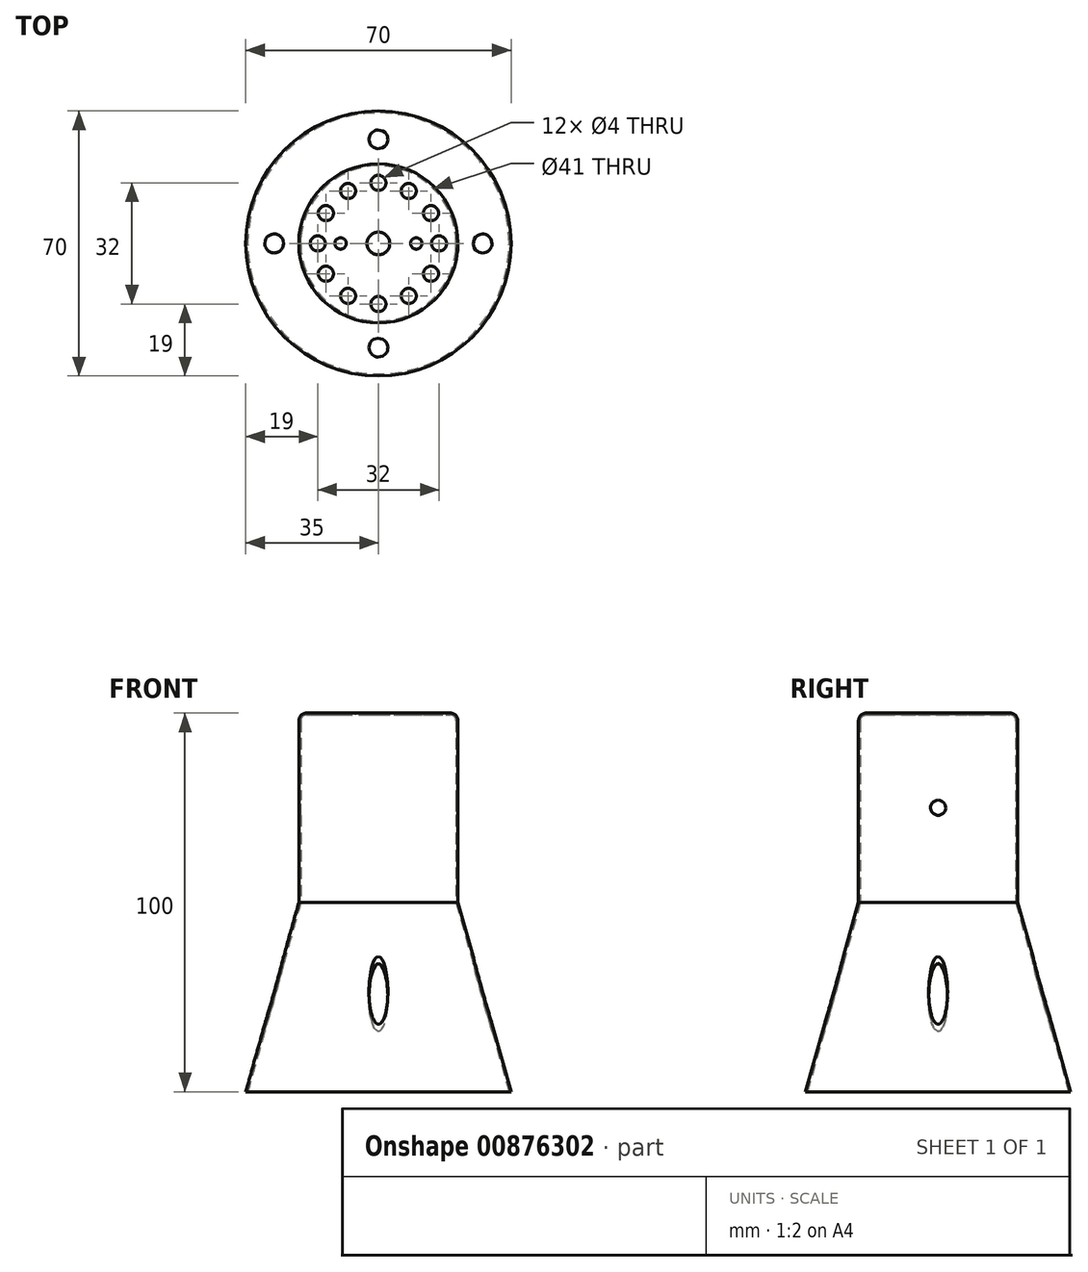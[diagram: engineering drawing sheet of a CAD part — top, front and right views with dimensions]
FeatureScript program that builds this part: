
annotation { "Feature Type Name" : "Feature", "Feature Type Description" : "" }
export const myFeature = defineFeature(function(context is Context, id is Id, definition is map)
    precondition{}
    {
        {
            var Q0;
            Q0=qCreatedBy(makeId("Front.planeOp"),FACE);
            var sketch = newSketch(context, id + "F0", { "sketchPlane" : qUnion([Q0])});
            skLineSegment(sketch, "E0", {"start": v(0, 0) * mm, "end": v(0, 50) * mm});
            skLineSegment(sketch, "E1", {"start": v(0, 0) * mm, "end": v(0, -50) * mm});
            skLineSegment(sketch, "E2.bottom", {"start": v(35, 0) * mm, "end": v(-35, 0) * mm});
            skLineSegment(sketch, "E2.top", {"start": v(35, -50) * mm, "end": v(-35, -50) * mm});
            skLineSegment(sketch, "E2.left", {"start": v(35, 0) * mm, "end": v(35, -50) * mm});
            skLineSegment(sketch, "E2.right", {"start": v(-35, 0) * mm, "end": v(-35, -50) * mm});
            skPoint(sketch, "E2.middle", {"position": v(0, -25) * mm});
            skLineSegment(sketch, "E3.bottom", {"start": v(21, 50) * mm, "end": v(-21, 50) * mm});
            skLineSegment(sketch, "E3.top", {"start": v(21, 0) * mm, "end": v(-21, 0) * mm});
            skLineSegment(sketch, "E3.left", {"start": v(21, 50) * mm, "end": v(21, 0) * mm});
            skLineSegment(sketch, "E3.right", {"start": v(-21, 50) * mm, "end": v(-21, 0) * mm});
            skPoint(sketch, "E3.middle", {"position": v(0, 25) * mm});
            skLineSegment(sketch, "E4", {"start": v(-21, 0) * mm, "end": v(-35, -50) * mm});
            skLineSegment(sketch, "E5", {"start": v(21, 0) * mm, "end": v(35, -50) * mm});
            skSolve(sketch);
        }
        {
            var Q0;
            {var subQ0=sQuery(id+"F0.wireOp",EDGE,"E0");Q0=makeQuery(id+"F0.imprint","IMPRINT",FACE,{"disambiguationData":[TD([[makeQuery(id+"F0.imprint","IMPRINT",EDGE,{"derivedFrom":subQ0}),1.0]])]});}
            var Q1;
            {var subQ0=sQuery(id+"F0.wireOp",EDGE,"E1");Q1=makeQuery(id+"F0.imprint","IMPRINT",FACE,{"disambiguationData":[TD([[makeQuery(id+"F0.imprint","IMPRINT",EDGE,{"derivedFrom":subQ0}),-1.0]])]});}
            var Q2;
            Q2=sQuery(id+"F0.wireOp",EDGE,"E3.right");
            var Q3;
            Q3=sQuery(id+"F0.wireOp",EDGE,"E4");
            var Q4;
            Q4=sQuery(id+"F0.wireOp",EDGE,"E0");
            revolve(context, id + "F1", {"surfaceOperationType" : NewSurfaceOperationType.NEW, "entities" : qUnion([Q0, Q1]), "surfaceEntities" : qUnion([Q2, Q3]), "axis" : qUnion([Q4]), "revolveType" : RevolveType.FULL});
        }
        {
            var Q0;
            Q0=makeQuery(id+"F1.opRevolve","SWEPT_EDGE",EDGE,{"disambiguationData":[OSD([sQuery(id+"F0.wireOp",EDGE,"E3.bottom"),sQuery(id+"F0.wireOp",EDGE,"E3.right")])]});
            fillet(context, id + "F2", {"entities" : qUnion([Q0]), "radius" : 2 * mm, "tangentPropagation" : true, "allowEdgeOverflow" : false});
        }
        {
            var Q0;
            Q0=makeQuery(id+"F1.opRevolve","SWEPT_FACE",FACE,{"disambiguationData":[OSD([sQuery(id+"F0.wireOp",EDGE,"E2.top")])]});
            shell(context, id + "F3", {"entities" : qUnion([Q0]), "thickness" : 0.5 * mm});
        }
        {
            var Q0;
            Q0=qCreatedBy(makeId("Top.planeOp"),FACE);
            var sketch = newSketch(context, id + "F4", { "sketchPlane" : qUnion([Q0])});
            skCircle(sketch, "E6", {"center": v(0, 0) * mm, "radius": 27.5 * mm});
            skCircle(sketch, "E7", {"center": v(0, 27.5) * mm, "radius": 2.5 * mm});
            skCircle(sketch, "E8", {"center": v(0, -27.5) * mm, "radius": 2.5 * mm});
            skCircle(sketch, "E9", {"center": v(27.5, 0) * mm, "radius": 2.5 * mm});
            skCircle(sketch, "E10", {"center": v(-27.5, 0) * mm, "radius": 2.5 * mm});
            skSolve(sketch);
        }
        {
            var Q0;
            {var subQ0=sQuery(id+"F4.wireOp",EDGE,"E7");var subQ1=sQuery(id+"F4.wireOp",EDGE,"E6");var subQ2=makeQuery(id+"F4.imprint","INTERSECT",VERTEX,{"disambiguationData":[OD(0.0)],"derivedFrom":[subQ1,subQ0]});Q0=makeQuery(id+"F4.imprint","IMPRINT",FACE,{"disambiguationData":[TD([[makeQuery(id+"F4.imprint","IMPRINT",EDGE,{"disambiguationData":[TD([[subQ2,-1.0]])],"derivedFrom":subQ1}),-1.0]])]});}
            var Q1;
            {var subQ0=sQuery(id+"F4.wireOp",EDGE,"E7");var subQ1=sQuery(id+"F4.wireOp",EDGE,"E6");var subQ2=makeQuery(id+"F4.imprint","INTERSECT",VERTEX,{"disambiguationData":[OD(0.0)],"derivedFrom":[subQ1,subQ0]});Q1=makeQuery(id+"F4.imprint","IMPRINT",FACE,{"disambiguationData":[TD([[makeQuery(id+"F4.imprint","IMPRINT",EDGE,{"disambiguationData":[TD([[subQ2,-1.0]])],"derivedFrom":subQ1}),1.0]])]});}
            var Q2;
            {var subQ0=sQuery(id+"F4.wireOp",EDGE,"E10");var subQ1=sQuery(id+"F4.wireOp",EDGE,"E6");var subQ2=makeQuery(id+"F4.imprint","INTERSECT",VERTEX,{"disambiguationData":[OD(0.0)],"derivedFrom":[subQ1,subQ0]});Q2=makeQuery(id+"F4.imprint","IMPRINT",FACE,{"disambiguationData":[TD([[makeQuery(id+"F4.imprint","IMPRINT",EDGE,{"disambiguationData":[TD([[subQ2,-1.0]])],"derivedFrom":subQ1}),1.0]])]});}
            var Q3;
            {var subQ0=sQuery(id+"F4.wireOp",EDGE,"E10");var subQ1=sQuery(id+"F4.wireOp",EDGE,"E6");var subQ2=makeQuery(id+"F4.imprint","INTERSECT",VERTEX,{"disambiguationData":[OD(0.0)],"derivedFrom":[subQ1,subQ0]});Q3=makeQuery(id+"F4.imprint","IMPRINT",FACE,{"disambiguationData":[TD([[makeQuery(id+"F4.imprint","IMPRINT",EDGE,{"disambiguationData":[TD([[subQ2,-1.0]])],"derivedFrom":subQ1}),-1.0]])]});}
            var Q4;
            {var subQ0=sQuery(id+"F4.wireOp",EDGE,"E9");var subQ1=sQuery(id+"F4.wireOp",EDGE,"E6");var subQ2=makeQuery(id+"F4.imprint","INTERSECT",VERTEX,{"disambiguationData":[OD(0.0)],"derivedFrom":[subQ1,subQ0]});Q4=makeQuery(id+"F4.imprint","IMPRINT",FACE,{"disambiguationData":[TD([[makeQuery(id+"F4.imprint","IMPRINT",EDGE,{"disambiguationData":[TD([[subQ2,1.0]])],"derivedFrom":subQ1}),1.0]])]});}
            var Q5;
            {var subQ0=sQuery(id+"F4.wireOp",EDGE,"E9");var subQ1=sQuery(id+"F4.wireOp",EDGE,"E6");var subQ2=makeQuery(id+"F4.imprint","INTERSECT",VERTEX,{"disambiguationData":[OD(0.0)],"derivedFrom":[subQ1,subQ0]});Q5=makeQuery(id+"F4.imprint","IMPRINT",FACE,{"disambiguationData":[TD([[makeQuery(id+"F4.imprint","IMPRINT",EDGE,{"disambiguationData":[TD([[subQ2,1.0]])],"derivedFrom":subQ1}),-1.0]])]});}
            var Q6;
            {var subQ0=sQuery(id+"F4.wireOp",EDGE,"E8");var subQ1=sQuery(id+"F4.wireOp",EDGE,"E6");var subQ2=makeQuery(id+"F4.imprint","INTERSECT",VERTEX,{"disambiguationData":[OD(0.0)],"derivedFrom":[subQ1,subQ0]});Q6=makeQuery(id+"F4.imprint","IMPRINT",FACE,{"disambiguationData":[TD([[makeQuery(id+"F4.imprint","IMPRINT",EDGE,{"disambiguationData":[TD([[subQ2,-1.0]])],"derivedFrom":subQ1}),1.0]])]});}
            var Q7;
            {var subQ0=sQuery(id+"F4.wireOp",EDGE,"E8");var subQ1=sQuery(id+"F4.wireOp",EDGE,"E6");var subQ2=makeQuery(id+"F4.imprint","INTERSECT",VERTEX,{"disambiguationData":[OD(0.0)],"derivedFrom":[subQ1,subQ0]});Q7=makeQuery(id+"F4.imprint","IMPRINT",FACE,{"disambiguationData":[TD([[makeQuery(id+"F4.imprint","IMPRINT",EDGE,{"disambiguationData":[TD([[subQ2,-1.0]])],"derivedFrom":subQ1}),-1.0]])]});}
            extrude(context, id + "F5", {"entities" : qUnion([Q0, Q1, Q2, Q3, Q4, Q5, Q6, Q7]), "operationType" : NewBodyOperationType.REMOVE, "oppositeDirection" : true, "depth" : 63.2 * mm, "offsetDistance" : 25 * mm});
        }
        {
            var Q0;
            Q0=makeQuery(id+"F1.opRevolve","SWEPT_FACE",FACE,{"disambiguationData":[OSD([sQuery(id+"F0.wireOp",EDGE,"E3.bottom")])]});
            var sketch = newSketch(context, id + "F6", { "sketchPlane" : qUnion([Q0])});
            skCircle(sketch, "E11", {"center": v(0, 0) * mm, "radius": 3 * mm});
            skLineSegment(sketch, "E12", {"start": v(0, 0) * mm, "end": v(10, 0) * mm});
            skLineSegment(sketch, "E13", {"start": v(0, 0) * mm, "end": v(-10, 0) * mm});
            skCircle(sketch, "E14", {"center": v(10, 0) * mm, "radius": 1.5 * mm});
            skCircle(sketch, "E15", {"center": v(-10, 0) * mm, "radius": 1.5 * mm});
            skCircle(sketch, "E16", {"center": v(0, 0) * mm, "radius": 16 * mm});
            skCircle(sketch, "E17", {"center": v(0, 16) * mm, "radius": 2 * mm});
            skCircle(sketch, "E18", {"center": v(0, -16) * mm, "radius": 2 * mm});
            skCircle(sketch, "E19", {"center": v(16, 0) * mm, "radius": 2 * mm});
            skCircle(sketch, "E20", {"center": v(-16, 0) * mm, "radius": 2 * mm});
            skLineSegment(sketch, "E21", {"start": v(0, 0) * mm, "end": v(-13.86, 8) * mm});
            skCircle(sketch, "E22", {"center": v(-13.86, 8) * mm, "radius": 2 * mm});
            skLineSegment(sketch, "E23", {"start": v(0, 0) * mm, "end": v(-8, 13.86) * mm});
            skCircle(sketch, "E24", {"center": v(-8, 13.86) * mm, "radius": 2 * mm});
            skLineSegment(sketch, "E25", {"start": v(0, 0) * mm, "end": v(8, 13.86) * mm});
            skCircle(sketch, "E26", {"center": v(8, 13.86) * mm, "radius": 2 * mm});
            skLineSegment(sketch, "E27", {"start": v(0, 0) * mm, "end": v(13.86, 8) * mm});
            skCircle(sketch, "E28", {"center": v(13.86, 8) * mm, "radius": 2 * mm});
            skLineSegment(sketch, "E29", {"start": v(0, 0) * mm, "end": v(13.86, -8) * mm});
            skCircle(sketch, "E30", {"center": v(13.86, -8) * mm, "radius": 2 * mm});
            skLineSegment(sketch, "E31", {"start": v(0, 0) * mm, "end": v(8, -13.86) * mm});
            skCircle(sketch, "E32", {"center": v(8, -13.86) * mm, "radius": 2 * mm});
            skLineSegment(sketch, "E33", {"start": v(0, 0) * mm, "end": v(-8, -13.86) * mm});
            skCircle(sketch, "E34", {"center": v(-8, -13.86) * mm, "radius": 2 * mm});
            skLineSegment(sketch, "E35", {"start": v(0, 0) * mm, "end": v(-13.86, -8) * mm});
            skCircle(sketch, "E36", {"center": v(-13.86, -8) * mm, "radius": 2 * mm});
            skSolve(sketch);
        }
        {
            var Q0;
            {var subQ0=sQuery(id+"F6.wireOp",EDGE,"E17");var subQ1=sQuery(id+"F6.wireOp",EDGE,"E16");var subQ2=makeQuery(id+"F6.imprint","INTERSECT",VERTEX,{"disambiguationData":[OD(0.0)],"derivedFrom":[subQ1,subQ0]});Q0=makeQuery(id+"F6.imprint","IMPRINT",FACE,{"disambiguationData":[TD([[makeQuery(id+"F6.imprint","IMPRINT",EDGE,{"disambiguationData":[TD([[subQ2,-1.0]])],"derivedFrom":subQ1}),1.0]])]});}
            var Q1;
            {var subQ0=sQuery(id+"F6.wireOp",EDGE,"E17");var subQ1=sQuery(id+"F6.wireOp",EDGE,"E16");var subQ2=makeQuery(id+"F6.imprint","INTERSECT",VERTEX,{"disambiguationData":[OD(0.0)],"derivedFrom":[subQ1,subQ0]});Q1=makeQuery(id+"F6.imprint","IMPRINT",FACE,{"disambiguationData":[TD([[makeQuery(id+"F6.imprint","IMPRINT",EDGE,{"disambiguationData":[TD([[subQ2,-1.0]])],"derivedFrom":subQ1}),-1.0]])]});}
            var Q2;
            {var subQ0=sQuery(id+"F6.wireOp",EDGE,"E20");var subQ1=sQuery(id+"F6.wireOp",EDGE,"E16");var subQ2=makeQuery(id+"F6.imprint","INTERSECT",VERTEX,{"disambiguationData":[OD(0.0)],"derivedFrom":[subQ1,subQ0]});Q2=makeQuery(id+"F6.imprint","IMPRINT",FACE,{"disambiguationData":[TD([[makeQuery(id+"F6.imprint","IMPRINT",EDGE,{"disambiguationData":[TD([[subQ2,-1.0]])],"derivedFrom":subQ1}),-1.0]])]});}
            var Q3;
            {var subQ0=sQuery(id+"F6.wireOp",EDGE,"E20");var subQ1=sQuery(id+"F6.wireOp",EDGE,"E16");var subQ2=makeQuery(id+"F6.imprint","INTERSECT",VERTEX,{"disambiguationData":[OD(0.0)],"derivedFrom":[subQ1,subQ0]});Q3=makeQuery(id+"F6.imprint","IMPRINT",FACE,{"disambiguationData":[TD([[makeQuery(id+"F6.imprint","IMPRINT",EDGE,{"disambiguationData":[TD([[subQ2,-1.0]])],"derivedFrom":subQ1}),1.0]])]});}
            var Q4;
            {var subQ0=sQuery(id+"F6.wireOp",EDGE,"E18");var subQ1=sQuery(id+"F6.wireOp",EDGE,"E16");var subQ2=makeQuery(id+"F6.imprint","INTERSECT",VERTEX,{"disambiguationData":[OD(0.0)],"derivedFrom":[subQ1,subQ0]});Q4=makeQuery(id+"F6.imprint","IMPRINT",FACE,{"disambiguationData":[TD([[makeQuery(id+"F6.imprint","IMPRINT",EDGE,{"disambiguationData":[TD([[subQ2,-1.0]])],"derivedFrom":subQ1}),1.0]])]});}
            var Q5;
            {var subQ0=sQuery(id+"F6.wireOp",EDGE,"E18");var subQ1=sQuery(id+"F6.wireOp",EDGE,"E16");var subQ2=makeQuery(id+"F6.imprint","INTERSECT",VERTEX,{"disambiguationData":[OD(0.0)],"derivedFrom":[subQ1,subQ0]});Q5=makeQuery(id+"F6.imprint","IMPRINT",FACE,{"disambiguationData":[TD([[makeQuery(id+"F6.imprint","IMPRINT",EDGE,{"disambiguationData":[TD([[subQ2,-1.0]])],"derivedFrom":subQ1}),-1.0]])]});}
            var Q6;
            {var subQ0=sQuery(id+"F6.wireOp",EDGE,"E19");var subQ1=sQuery(id+"F6.wireOp",EDGE,"E16");var subQ2=makeQuery(id+"F6.imprint","INTERSECT",VERTEX,{"disambiguationData":[OD(0.0)],"derivedFrom":[subQ1,subQ0]});Q6=makeQuery(id+"F6.imprint","IMPRINT",FACE,{"disambiguationData":[TD([[makeQuery(id+"F6.imprint","IMPRINT",EDGE,{"disambiguationData":[TD([[subQ2,1.0]])],"derivedFrom":subQ1}),1.0]])]});}
            var Q7;
            {var subQ0=sQuery(id+"F6.wireOp",EDGE,"E19");var subQ1=sQuery(id+"F6.wireOp",EDGE,"E16");var subQ2=makeQuery(id+"F6.imprint","INTERSECT",VERTEX,{"disambiguationData":[OD(0.0)],"derivedFrom":[subQ1,subQ0]});Q7=makeQuery(id+"F6.imprint","IMPRINT",FACE,{"disambiguationData":[TD([[makeQuery(id+"F6.imprint","IMPRINT",EDGE,{"disambiguationData":[TD([[subQ2,1.0]])],"derivedFrom":subQ1}),-1.0]])]});}
            var Q8;
            {var subQ0=sQuery(id+"F6.wireOp",EDGE,"E16");var subQ1=makeQuery(id+"F6.imprint","INTERSECT",VERTEX,{"derivedFrom":[subQ0,sQuery(id+"F6.wireOp",EDGE,"E27")]});Q8=makeQuery(id+"F6.imprint","IMPRINT",FACE,{"disambiguationData":[TD([[makeQuery(id+"F6.imprint","IMPRINT",EDGE,{"disambiguationData":[TD([[subQ1,1.0]])],"derivedFrom":subQ0}),-1.0]])]});}
            var Q9;
            {var subQ0=sQuery(id+"F6.wireOp",EDGE,"E27");var subQ1=sQuery(id+"F6.wireOp",EDGE,"E16");var subQ2=makeQuery(id+"F6.imprint","INTERSECT",VERTEX,{"derivedFrom":[subQ1,subQ0]});Q9=makeQuery(id+"F6.imprint","IMPRINT",FACE,{"disambiguationData":[TD([[makeQuery(id+"F6.imprint","IMPRINT",EDGE,{"disambiguationData":[TD([[subQ2,1.0]])],"derivedFrom":subQ1}),1.0]])]});}
            var Q10;
            {var subQ0=sQuery(id+"F6.wireOp",EDGE,"E27");var subQ1=sQuery(id+"F6.wireOp",EDGE,"E16");var subQ2=makeQuery(id+"F6.imprint","INTERSECT",VERTEX,{"derivedFrom":[subQ1,subQ0]});Q10=makeQuery(id+"F6.imprint","IMPRINT",FACE,{"disambiguationData":[TD([[makeQuery(id+"F6.imprint","IMPRINT",EDGE,{"disambiguationData":[TD([[subQ2,-1.0]])],"derivedFrom":subQ1}),1.0]])]});}
            var Q11;
            {var subQ0=sQuery(id+"F6.wireOp",EDGE,"E16");var subQ1=makeQuery(id+"F6.imprint","INTERSECT",VERTEX,{"derivedFrom":[subQ0,sQuery(id+"F6.wireOp",EDGE,"E25")]});Q11=makeQuery(id+"F6.imprint","IMPRINT",FACE,{"disambiguationData":[TD([[makeQuery(id+"F6.imprint","IMPRINT",EDGE,{"disambiguationData":[TD([[subQ1,1.0]])],"derivedFrom":subQ0}),-1.0]])]});}
            var Q12;
            {var subQ0=sQuery(id+"F6.wireOp",EDGE,"E25");var subQ1=sQuery(id+"F6.wireOp",EDGE,"E16");var subQ2=makeQuery(id+"F6.imprint","INTERSECT",VERTEX,{"derivedFrom":[subQ1,subQ0]});Q12=makeQuery(id+"F6.imprint","IMPRINT",FACE,{"disambiguationData":[TD([[makeQuery(id+"F6.imprint","IMPRINT",EDGE,{"disambiguationData":[TD([[subQ2,1.0]])],"derivedFrom":subQ1}),1.0]])]});}
            var Q13;
            {var subQ0=sQuery(id+"F6.wireOp",EDGE,"E25");var subQ1=sQuery(id+"F6.wireOp",EDGE,"E16");var subQ2=makeQuery(id+"F6.imprint","INTERSECT",VERTEX,{"derivedFrom":[subQ1,subQ0]});Q13=makeQuery(id+"F6.imprint","IMPRINT",FACE,{"disambiguationData":[TD([[makeQuery(id+"F6.imprint","IMPRINT",EDGE,{"disambiguationData":[TD([[subQ2,-1.0]])],"derivedFrom":subQ1}),1.0]])]});}
            var Q14;
            {var subQ0=sQuery(id+"F6.wireOp",EDGE,"E16");var subQ1=makeQuery(id+"F6.imprint","INTERSECT",VERTEX,{"derivedFrom":[subQ0,sQuery(id+"F6.wireOp",EDGE,"E23")]});Q14=makeQuery(id+"F6.imprint","IMPRINT",FACE,{"disambiguationData":[TD([[makeQuery(id+"F6.imprint","IMPRINT",EDGE,{"disambiguationData":[TD([[subQ1,1.0]])],"derivedFrom":subQ0}),-1.0]])]});}
            var Q15;
            {var subQ0=sQuery(id+"F6.wireOp",EDGE,"E23");var subQ1=sQuery(id+"F6.wireOp",EDGE,"E16");var subQ2=makeQuery(id+"F6.imprint","INTERSECT",VERTEX,{"derivedFrom":[subQ1,subQ0]});Q15=makeQuery(id+"F6.imprint","IMPRINT",FACE,{"disambiguationData":[TD([[makeQuery(id+"F6.imprint","IMPRINT",EDGE,{"disambiguationData":[TD([[subQ2,1.0]])],"derivedFrom":subQ1}),1.0]])]});}
            var Q16;
            {var subQ0=sQuery(id+"F6.wireOp",EDGE,"E23");var subQ1=sQuery(id+"F6.wireOp",EDGE,"E16");var subQ2=makeQuery(id+"F6.imprint","INTERSECT",VERTEX,{"derivedFrom":[subQ1,subQ0]});Q16=makeQuery(id+"F6.imprint","IMPRINT",FACE,{"disambiguationData":[TD([[makeQuery(id+"F6.imprint","IMPRINT",EDGE,{"disambiguationData":[TD([[subQ2,-1.0]])],"derivedFrom":subQ1}),1.0]])]});}
            var Q17;
            {var subQ0=sQuery(id+"F6.wireOp",EDGE,"E16");var subQ1=makeQuery(id+"F6.imprint","INTERSECT",VERTEX,{"derivedFrom":[subQ0,sQuery(id+"F6.wireOp",EDGE,"E21")]});Q17=makeQuery(id+"F6.imprint","IMPRINT",FACE,{"disambiguationData":[TD([[makeQuery(id+"F6.imprint","IMPRINT",EDGE,{"disambiguationData":[TD([[subQ1,1.0]])],"derivedFrom":subQ0}),-1.0]])]});}
            var Q18;
            {var subQ0=sQuery(id+"F6.wireOp",EDGE,"E21");var subQ1=sQuery(id+"F6.wireOp",EDGE,"E16");var subQ2=makeQuery(id+"F6.imprint","INTERSECT",VERTEX,{"derivedFrom":[subQ1,subQ0]});Q18=makeQuery(id+"F6.imprint","IMPRINT",FACE,{"disambiguationData":[TD([[makeQuery(id+"F6.imprint","IMPRINT",EDGE,{"disambiguationData":[TD([[subQ2,1.0]])],"derivedFrom":subQ1}),1.0]])]});}
            var Q19;
            {var subQ0=sQuery(id+"F6.wireOp",EDGE,"E21");var subQ1=sQuery(id+"F6.wireOp",EDGE,"E16");var subQ2=makeQuery(id+"F6.imprint","INTERSECT",VERTEX,{"derivedFrom":[subQ1,subQ0]});Q19=makeQuery(id+"F6.imprint","IMPRINT",FACE,{"disambiguationData":[TD([[makeQuery(id+"F6.imprint","IMPRINT",EDGE,{"disambiguationData":[TD([[subQ2,-1.0]])],"derivedFrom":subQ1}),1.0]])]});}
            var Q20;
            {var subQ0=sQuery(id+"F6.wireOp",EDGE,"E16");var subQ1=makeQuery(id+"F6.imprint","INTERSECT",VERTEX,{"derivedFrom":[subQ0,sQuery(id+"F6.wireOp",EDGE,"E35")]});Q20=makeQuery(id+"F6.imprint","IMPRINT",FACE,{"disambiguationData":[TD([[makeQuery(id+"F6.imprint","IMPRINT",EDGE,{"disambiguationData":[TD([[subQ1,1.0]])],"derivedFrom":subQ0}),-1.0]])]});}
            var Q21;
            {var subQ0=sQuery(id+"F6.wireOp",EDGE,"E35");var subQ1=sQuery(id+"F6.wireOp",EDGE,"E16");var subQ2=makeQuery(id+"F6.imprint","INTERSECT",VERTEX,{"derivedFrom":[subQ1,subQ0]});Q21=makeQuery(id+"F6.imprint","IMPRINT",FACE,{"disambiguationData":[TD([[makeQuery(id+"F6.imprint","IMPRINT",EDGE,{"disambiguationData":[TD([[subQ2,1.0]])],"derivedFrom":subQ1}),1.0]])]});}
            var Q22;
            {var subQ0=sQuery(id+"F6.wireOp",EDGE,"E35");var subQ1=sQuery(id+"F6.wireOp",EDGE,"E16");var subQ2=makeQuery(id+"F6.imprint","INTERSECT",VERTEX,{"derivedFrom":[subQ1,subQ0]});Q22=makeQuery(id+"F6.imprint","IMPRINT",FACE,{"disambiguationData":[TD([[makeQuery(id+"F6.imprint","IMPRINT",EDGE,{"disambiguationData":[TD([[subQ2,-1.0]])],"derivedFrom":subQ1}),1.0]])]});}
            var Q23;
            {var subQ0=sQuery(id+"F6.wireOp",EDGE,"E16");var subQ1=makeQuery(id+"F6.imprint","INTERSECT",VERTEX,{"derivedFrom":[subQ0,sQuery(id+"F6.wireOp",EDGE,"E33")]});Q23=makeQuery(id+"F6.imprint","IMPRINT",FACE,{"disambiguationData":[TD([[makeQuery(id+"F6.imprint","IMPRINT",EDGE,{"disambiguationData":[TD([[subQ1,1.0]])],"derivedFrom":subQ0}),-1.0]])]});}
            var Q24;
            {var subQ0=sQuery(id+"F6.wireOp",EDGE,"E33");var subQ1=sQuery(id+"F6.wireOp",EDGE,"E16");var subQ2=makeQuery(id+"F6.imprint","INTERSECT",VERTEX,{"derivedFrom":[subQ1,subQ0]});Q24=makeQuery(id+"F6.imprint","IMPRINT",FACE,{"disambiguationData":[TD([[makeQuery(id+"F6.imprint","IMPRINT",EDGE,{"disambiguationData":[TD([[subQ2,1.0]])],"derivedFrom":subQ1}),1.0]])]});}
            var Q25;
            {var subQ0=sQuery(id+"F6.wireOp",EDGE,"E33");var subQ1=sQuery(id+"F6.wireOp",EDGE,"E16");var subQ2=makeQuery(id+"F6.imprint","INTERSECT",VERTEX,{"derivedFrom":[subQ1,subQ0]});Q25=makeQuery(id+"F6.imprint","IMPRINT",FACE,{"disambiguationData":[TD([[makeQuery(id+"F6.imprint","IMPRINT",EDGE,{"disambiguationData":[TD([[subQ2,-1.0]])],"derivedFrom":subQ1}),1.0]])]});}
            var Q26;
            {var subQ0=sQuery(id+"F6.wireOp",EDGE,"E16");var subQ1=makeQuery(id+"F6.imprint","INTERSECT",VERTEX,{"derivedFrom":[subQ0,sQuery(id+"F6.wireOp",EDGE,"E31")]});Q26=makeQuery(id+"F6.imprint","IMPRINT",FACE,{"disambiguationData":[TD([[makeQuery(id+"F6.imprint","IMPRINT",EDGE,{"disambiguationData":[TD([[subQ1,1.0]])],"derivedFrom":subQ0}),-1.0]])]});}
            var Q27;
            {var subQ0=sQuery(id+"F6.wireOp",EDGE,"E31");var subQ1=sQuery(id+"F6.wireOp",EDGE,"E16");var subQ2=makeQuery(id+"F6.imprint","INTERSECT",VERTEX,{"derivedFrom":[subQ1,subQ0]});Q27=makeQuery(id+"F6.imprint","IMPRINT",FACE,{"disambiguationData":[TD([[makeQuery(id+"F6.imprint","IMPRINT",EDGE,{"disambiguationData":[TD([[subQ2,1.0]])],"derivedFrom":subQ1}),1.0]])]});}
            var Q28;
            {var subQ0=sQuery(id+"F6.wireOp",EDGE,"E31");var subQ1=sQuery(id+"F6.wireOp",EDGE,"E16");var subQ2=makeQuery(id+"F6.imprint","INTERSECT",VERTEX,{"derivedFrom":[subQ1,subQ0]});Q28=makeQuery(id+"F6.imprint","IMPRINT",FACE,{"disambiguationData":[TD([[makeQuery(id+"F6.imprint","IMPRINT",EDGE,{"disambiguationData":[TD([[subQ2,-1.0]])],"derivedFrom":subQ1}),1.0]])]});}
            var Q29;
            {var subQ0=sQuery(id+"F6.wireOp",EDGE,"E16");var subQ1=makeQuery(id+"F6.imprint","INTERSECT",VERTEX,{"derivedFrom":[subQ0,sQuery(id+"F6.wireOp",EDGE,"E29")]});Q29=makeQuery(id+"F6.imprint","IMPRINT",FACE,{"disambiguationData":[TD([[makeQuery(id+"F6.imprint","IMPRINT",EDGE,{"disambiguationData":[TD([[subQ1,1.0]])],"derivedFrom":subQ0}),-1.0]])]});}
            var Q30;
            {var subQ0=sQuery(id+"F6.wireOp",EDGE,"E29");var subQ1=sQuery(id+"F6.wireOp",EDGE,"E16");var subQ2=makeQuery(id+"F6.imprint","INTERSECT",VERTEX,{"derivedFrom":[subQ1,subQ0]});Q30=makeQuery(id+"F6.imprint","IMPRINT",FACE,{"disambiguationData":[TD([[makeQuery(id+"F6.imprint","IMPRINT",EDGE,{"disambiguationData":[TD([[subQ2,1.0]])],"derivedFrom":subQ1}),1.0]])]});}
            var Q31;
            {var subQ0=sQuery(id+"F6.wireOp",EDGE,"E29");var subQ1=sQuery(id+"F6.wireOp",EDGE,"E16");var subQ2=makeQuery(id+"F6.imprint","INTERSECT",VERTEX,{"derivedFrom":[subQ1,subQ0]});Q31=makeQuery(id+"F6.imprint","IMPRINT",FACE,{"disambiguationData":[TD([[makeQuery(id+"F6.imprint","IMPRINT",EDGE,{"disambiguationData":[TD([[subQ2,-1.0]])],"derivedFrom":subQ1}),1.0]])]});}
            var Q32;
            Q32=makeQuery(id+"F6.imprint","IMPRINT",FACE,{"disambiguationData":[TD([[makeQuery(id+"F6.imprint","IMPRINT",EDGE,{"derivedFrom":sQuery(id+"F6.wireOp",EDGE,"E15")}),1.0]])]});
            var Q33;
            {var subQ0=sQuery(id+"F6.wireOp",EDGE,"E13");var subQ1=sQuery(id+"F6.wireOp",EDGE,"E11");var subQ2=makeQuery(id+"F6.imprint","INTERSECT",VERTEX,{"derivedFrom":[subQ1,subQ0]});Q33=makeQuery(id+"F6.imprint","IMPRINT",FACE,{"disambiguationData":[TD([[makeQuery(id+"F6.imprint","IMPRINT",EDGE,{"disambiguationData":[TD([[subQ2,1.0]])],"derivedFrom":subQ1}),1.0]])]});}
            var Q34;
            {var subQ0=sQuery(id+"F6.wireOp",EDGE,"E23");var subQ1=sQuery(id+"F6.wireOp",EDGE,"E11");var subQ2=makeQuery(id+"F6.imprint","INTERSECT",VERTEX,{"derivedFrom":[subQ1,subQ0]});Q34=makeQuery(id+"F6.imprint","IMPRINT",FACE,{"disambiguationData":[TD([[makeQuery(id+"F6.imprint","IMPRINT",EDGE,{"disambiguationData":[TD([[subQ2,-1.0]])],"derivedFrom":subQ1}),1.0]])]});}
            var Q35;
            {var subQ0=sQuery(id+"F6.wireOp",EDGE,"E27");var subQ1=sQuery(id+"F6.wireOp",EDGE,"E11");var subQ2=makeQuery(id+"F6.imprint","INTERSECT",VERTEX,{"derivedFrom":[subQ1,subQ0]});Q35=makeQuery(id+"F6.imprint","IMPRINT",FACE,{"disambiguationData":[TD([[makeQuery(id+"F6.imprint","IMPRINT",EDGE,{"disambiguationData":[TD([[subQ2,-1.0]])],"derivedFrom":subQ1}),1.0]])]});}
            var Q36;
            {var subQ0=sQuery(id+"F6.wireOp",EDGE,"E12");var subQ1=sQuery(id+"F6.wireOp",EDGE,"E11");var subQ2=makeQuery(id+"F6.imprint","INTERSECT",VERTEX,{"derivedFrom":[subQ1,subQ0]});Q36=makeQuery(id+"F6.imprint","IMPRINT",FACE,{"disambiguationData":[TD([[makeQuery(id+"F6.imprint","IMPRINT",EDGE,{"disambiguationData":[TD([[subQ2,-1.0]])],"derivedFrom":subQ1}),1.0]])]});}
            var Q37;
            {var subQ0=sQuery(id+"F6.wireOp",EDGE,"E12");var subQ1=sQuery(id+"F6.wireOp",EDGE,"E11");var subQ2=makeQuery(id+"F6.imprint","INTERSECT",VERTEX,{"derivedFrom":[subQ1,subQ0]});Q37=makeQuery(id+"F6.imprint","IMPRINT",FACE,{"disambiguationData":[TD([[makeQuery(id+"F6.imprint","IMPRINT",EDGE,{"disambiguationData":[TD([[subQ2,1.0]])],"derivedFrom":subQ1}),1.0]])]});}
            var Q38;
            {var subQ0=sQuery(id+"F6.wireOp",EDGE,"E31");var subQ1=sQuery(id+"F6.wireOp",EDGE,"E11");var subQ2=makeQuery(id+"F6.imprint","INTERSECT",VERTEX,{"derivedFrom":[subQ1,subQ0]});Q38=makeQuery(id+"F6.imprint","IMPRINT",FACE,{"disambiguationData":[TD([[makeQuery(id+"F6.imprint","IMPRINT",EDGE,{"disambiguationData":[TD([[subQ2,-1.0]])],"derivedFrom":subQ1}),1.0]])]});}
            var Q39;
            {var subQ0=sQuery(id+"F6.wireOp",EDGE,"E35");var subQ1=sQuery(id+"F6.wireOp",EDGE,"E11");var subQ2=makeQuery(id+"F6.imprint","INTERSECT",VERTEX,{"derivedFrom":[subQ1,subQ0]});Q39=makeQuery(id+"F6.imprint","IMPRINT",FACE,{"disambiguationData":[TD([[makeQuery(id+"F6.imprint","IMPRINT",EDGE,{"disambiguationData":[TD([[subQ2,-1.0]])],"derivedFrom":subQ1}),1.0]])]});}
            var Q40;
            {var subQ0=sQuery(id+"F6.wireOp",EDGE,"E13");var subQ1=sQuery(id+"F6.wireOp",EDGE,"E11");var subQ2=makeQuery(id+"F6.imprint","INTERSECT",VERTEX,{"derivedFrom":[subQ1,subQ0]});Q40=makeQuery(id+"F6.imprint","IMPRINT",FACE,{"disambiguationData":[TD([[makeQuery(id+"F6.imprint","IMPRINT",EDGE,{"disambiguationData":[TD([[subQ2,-1.0]])],"derivedFrom":subQ1}),1.0]])]});}
            var Q41;
            {var subQ0=sQuery(id+"F6.wireOp",EDGE,"E33");var subQ1=sQuery(id+"F6.wireOp",EDGE,"E11");var subQ2=makeQuery(id+"F6.imprint","INTERSECT",VERTEX,{"derivedFrom":[subQ1,subQ0]});Q41=makeQuery(id+"F6.imprint","IMPRINT",FACE,{"disambiguationData":[TD([[makeQuery(id+"F6.imprint","IMPRINT",EDGE,{"disambiguationData":[TD([[subQ2,-1.0]])],"derivedFrom":subQ1}),1.0]])]});}
            var Q42;
            {var subQ0=sQuery(id+"F6.wireOp",EDGE,"E25");var subQ1=sQuery(id+"F6.wireOp",EDGE,"E11");var subQ2=makeQuery(id+"F6.imprint","INTERSECT",VERTEX,{"derivedFrom":[subQ1,subQ0]});Q42=makeQuery(id+"F6.imprint","IMPRINT",FACE,{"disambiguationData":[TD([[makeQuery(id+"F6.imprint","IMPRINT",EDGE,{"disambiguationData":[TD([[subQ2,-1.0]])],"derivedFrom":subQ1}),1.0]])]});}
            var Q43;
            Q43=makeQuery(id+"F6.imprint","IMPRINT",FACE,{"disambiguationData":[TD([[makeQuery(id+"F6.imprint","IMPRINT",EDGE,{"derivedFrom":sQuery(id+"F6.wireOp",EDGE,"E14")}),1.0]])]});
            extrude(context, id + "F7", {"entities" : qUnion([Q0, Q1, Q2, Q3, Q4, Q5, Q6, Q7, Q8, Q9, Q10, Q11, Q12, Q13, Q14, Q15, Q16, Q17, Q18, Q19, Q20, Q21, Q22, Q23, Q24, Q25, Q26, Q27, Q28, Q29, Q30, Q31, Q32, Q33, Q34, Q35, Q36, Q37, Q38, Q39, Q40, Q41, Q42, Q43]), "operationType" : NewBodyOperationType.REMOVE, "oppositeDirection" : true, "depth" : 2.2 * mm, "offsetDistance" : 25 * mm});
        }
        {
            var Q0;
            Q0=qCreatedBy(makeId("Right.planeOp"),FACE);
            var sketch = newSketch(context, id + "F8", { "sketchPlane" : qUnion([Q0])});
            skLineSegment(sketch, "E37", {"start": v(0, 0) * mm, "end": v(0, 25) * mm});
            skCircle(sketch, "E38", {"center": v(0, 25) * mm, "radius": 2 * mm});
            skSolve(sketch);
        }
        {
            var Q0;
            Q0 = qSketchRegion(id + "F8", true);
            extrude(context, id + "F9", {"entities" : qUnion([Q0]), "operationType" : NewBodyOperationType.REMOVE, "endBound" : BoundingType.SYMMETRIC, "depth" : 47.4 * mm, "offsetDistance" : 25 * mm});
        }
    });
